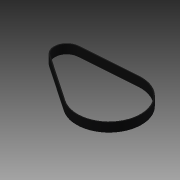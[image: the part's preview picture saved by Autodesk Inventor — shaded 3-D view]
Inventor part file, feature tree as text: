
AUTODESK INVENTOR PART (.ipt)
format: ipt  version: 2014 SP1 (Build 180222100, 222)  size: 102,912 bytes
history: native  units: in
note: dims shown in document units (in); Inventor stores cm internally (conversion verified against a paired STEP export)
features: other x3, sketch x1
ambient origin geometry x8: Origin, YZ Plane, XZ Plane, XY Plane, X Axis, Y Axis, Z Axis, Center Point
bodies: Solid1 (feature_tree)
feature tree (4):
  other  "belt.ipt"
  other  "Solid1::belt.ipt"
  other  "TaggingFeature1"
  sketch  "Sketch1"  dims[d0=0.3937in d1=2.5063in d4=0.9398in d8=2.4577in d11=0.3543in d12=0.0in d2=0.8661in d3=0.1693in d5=0.8661in d6=2.5984in d7=2.4577in d13=1.5748in d17=2.454in d18=1.9042in d15=360.0deg]
